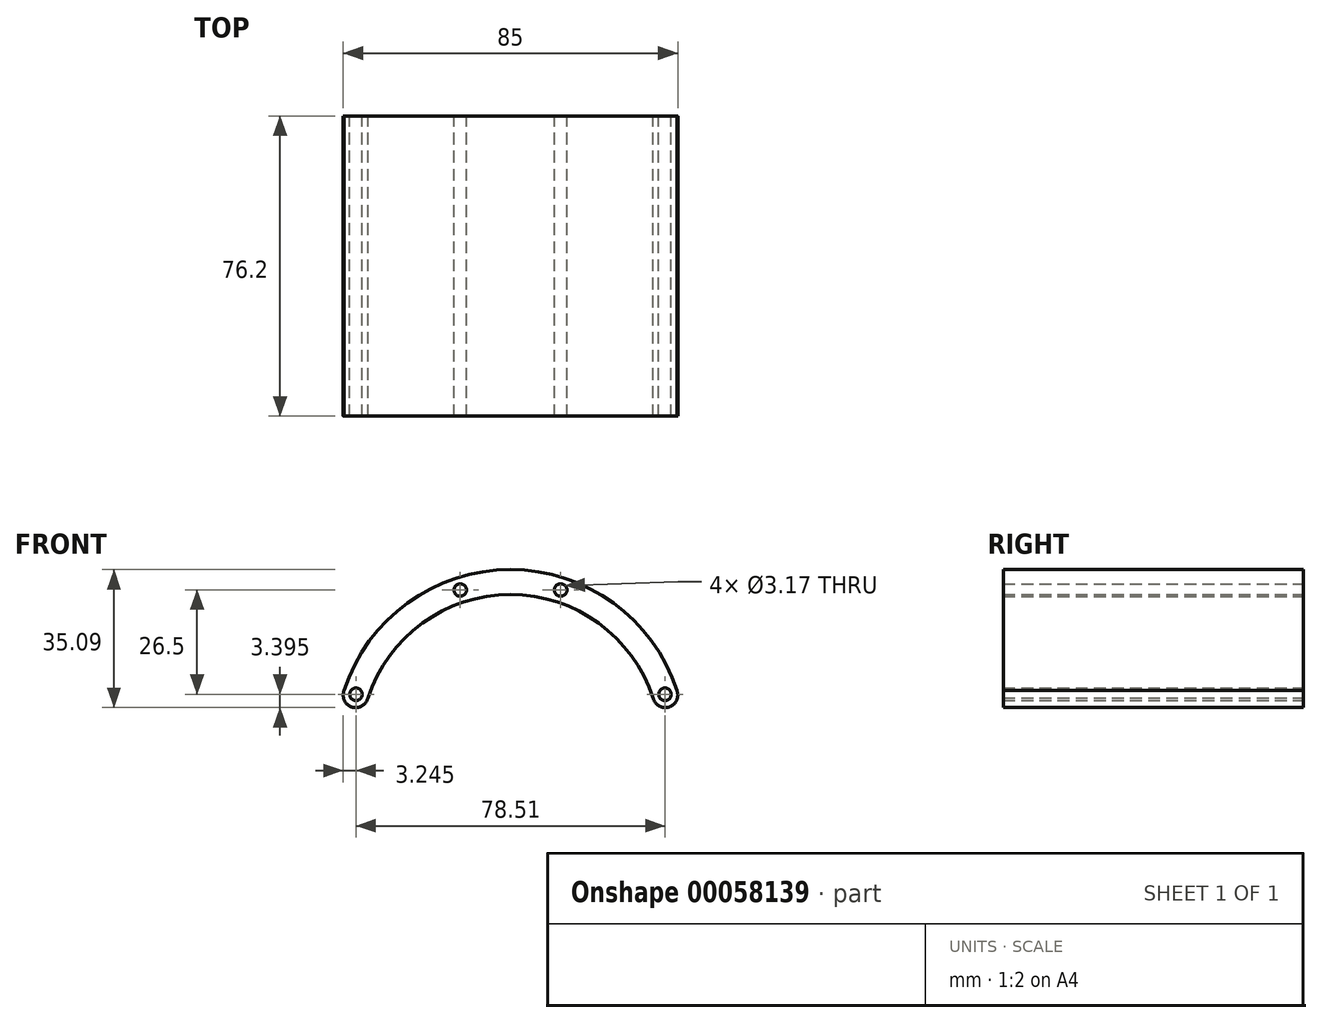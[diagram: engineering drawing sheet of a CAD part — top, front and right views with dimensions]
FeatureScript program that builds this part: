
annotation { "Feature Type Name" : "Feature", "Feature Type Description" : "" }
export const myFeature = defineFeature(function(context is Context, id is Id, definition is map)
    precondition{}
    {
        {
            var Q0;
            Q0=qCreatedBy(makeId("Front.planeOp"),FACE);
            var sketch = newSketch(context, id + "F0", { "sketchPlane" : qUnion([Q0])});
            skArc(sketch, "E0", {"start": v(42.42, 13.29) * mm, "mid": v(0, 44.45) * mm, "end": v(-42.42, 13.29) * mm});
            skArc(sketch, "E1", {"start": v(36.36, 11.39) * mm, "mid": v(0, 38.1) * mm, "end": v(-36.36, 11.39) * mm});
            skCircle(sketch, "E2", {"center": v(0, 0) * mm, "radius": 41.28 * mm, "construction": true});
            skLineSegment(sketch, "E3", {"start": v(0, 0) * mm, "end": v(66.09, 21.47) * mm, "construction": true});
            skLineSegment(sketch, "E4", {"start": v(0, 0) * mm, "end": v(-65, 21.12) * mm, "construction": true});
            skCircle(sketch, "E5", {"center": v(-39.25, 12.75) * mm, "radius": 1.59 * mm});
            skCircle(sketch, "E6", {"center": v(39.25, 12.75) * mm, "radius": 1.59 * mm});
            skLineSegment(sketch, "E7", {"start": v(0, 0) * mm, "end": v(-23.3, 71.72) * mm, "construction": true});
            skLineSegment(sketch, "E8", {"start": v(0, 0) * mm, "end": v(23.74, 73.06) * mm, "construction": true});
            skCircle(sketch, "E9", {"center": v(-12.75, 39.25) * mm, "radius": 1.59 * mm});
            skCircle(sketch, "E10", {"center": v(12.75, 39.25) * mm, "radius": 1.59 * mm});
            skArc(sketch, "E11", {"start": v(-42.27, 13.74) * mm, "mid": v(-40.3, 9.52) * mm, "end": v(-36.24, 11.77) * mm});
            skArc(sketch, "E12.MirrorCS", {"start": v(42.27, 13.74) * mm, "mid": v(40.3, 9.52) * mm, "end": v(36.24, 11.77) * mm});
            skSolve(sketch);
        }
        {
            var Q0;
            Q0 = qSketchRegion(id + "F0", true);
            extrude(context, id + "F1", {"entities" : qUnion([Q0]), "depth" : 76.2 * mm});
        }
    });
